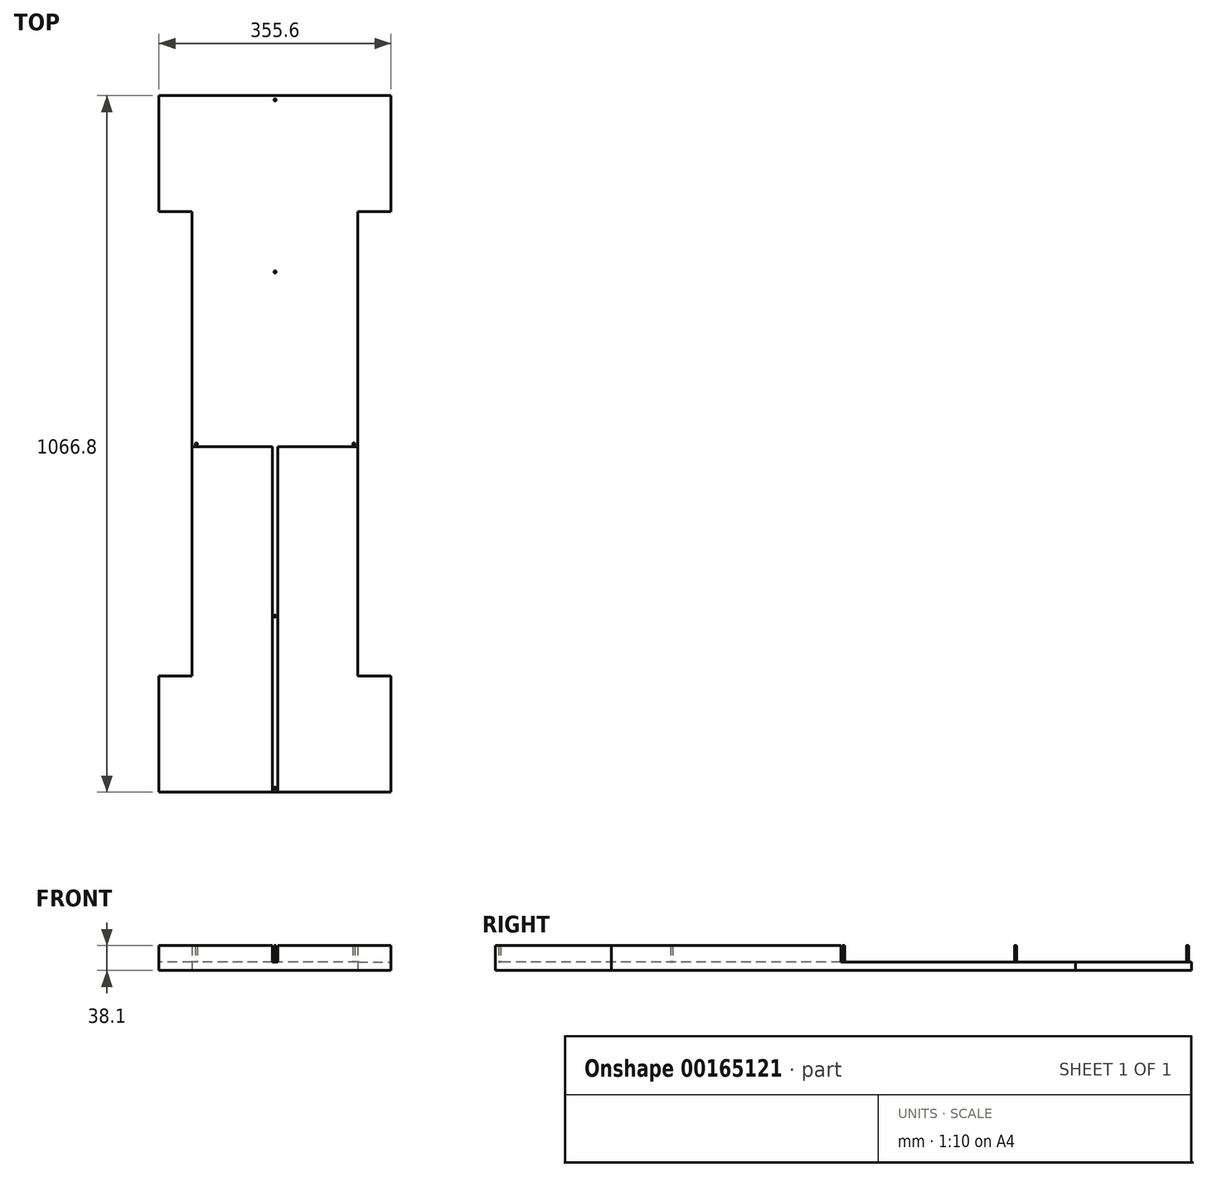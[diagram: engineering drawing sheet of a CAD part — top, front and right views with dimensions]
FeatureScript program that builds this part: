
annotation { "Feature Type Name" : "Feature", "Feature Type Description" : "" }
export const myFeature = defineFeature(function(context is Context, id is Id, definition is map)
    precondition{}
    {
        {
            var Q0;
            Q0=qCreatedBy(makeId("Top.planeOp"),FACE);
            var sketch = newSketch(context, id + "F0", { "sketchPlane" : qUnion([Q0])});
            skLineSegment(sketch, "E0", {"start": v(-127, 0) * mm, "end": v(127, 0) * mm, "construction": true});
            skLineSegment(sketch, "E1.left", {"start": v(-127, -355.6) * mm, "end": v(-127, 355.6) * mm});
            skLineSegment(sketch, "E1.right", {"start": v(127, -355.6) * mm, "end": v(127, 355.6) * mm});
            skLineSegment(sketch, "E2.bottom", {"start": v(-127, 355.6) * mm, "end": v(-177.8, 355.6) * mm});
            skLineSegment(sketch, "E2.top", {"start": v(177.8, 533.4) * mm, "end": v(-177.8, 533.4) * mm});
            skLineSegment(sketch, "E2.left", {"start": v(177.8, 355.6) * mm, "end": v(177.8, 533.4) * mm});
            skLineSegment(sketch, "E2.right", {"start": v(-177.8, 355.6) * mm, "end": v(-177.8, 533.4) * mm});
            skLineSegment(sketch, "E3", {"start": v(0, 0) * mm, "end": v(0, 533.4) * mm, "construction": true});
            skLineSegment(sketch, "E4", {"start": v(127, 355.6) * mm, "end": v(177.8, 355.6) * mm});
            skLineSegment(sketch, "E5", {"start": v(0, 0) * mm, "end": v(0, -533.4) * mm, "construction": true});
            skPoint(sketch, "E6.middle", {"position": v(0, 0) * mm});
            skLineSegment(sketch, "E7", {"start": v(-177.8, 444.5) * mm, "end": v(0, 444.5) * mm, "construction": true});
            skLineSegment(sketch, "E8", {"start": v(-127, -355.6) * mm, "end": v(-177.8, -355.6) * mm});
            skLineSegment(sketch, "E9", {"start": v(-177.8, -355.6) * mm, "end": v(-177.8, -533.4) * mm});
            skLineSegment(sketch, "E10", {"start": v(-177.8, -533.4) * mm, "end": v(177.8, -533.4) * mm});
            skLineSegment(sketch, "E11", {"start": v(177.8, -533.4) * mm, "end": v(177.8, -355.6) * mm});
            skLineSegment(sketch, "E12", {"start": v(177.8, -355.6) * mm, "end": v(127, -355.6) * mm});
            skSolve(sketch);
        }
        {
            var Q0;
            Q0=qSketchRegion(id+"F0",true);
            extrude(context, id + "F1", {"entities" : qUnion([Q0]), "depth" : 12.7 * mm});
        }
        {
            var Q0;
            Q0=makeQuery(id+"F1.opExtrude","CAP_FACE",FACE,{"disambiguationData":[OSD([sQuery(id+"F0.wireOp",EDGE,"E1.left"),sQuery(id+"F0.wireOp",EDGE,"E1.right"),sQuery(id+"F0.wireOp",EDGE,"E2.bottom"),sQuery(id+"F0.wireOp",EDGE,"E2.top"),sQuery(id+"F0.wireOp",EDGE,"E2.left"),sQuery(id+"F0.wireOp",EDGE,"E2.right"),sQuery(id+"F0.wireOp",EDGE,"E4"),sQuery(id+"F0.wireOp",EDGE,"E8"),sQuery(id+"F0.wireOp",EDGE,"E9"),sQuery(id+"F0.wireOp",EDGE,"E10"),sQuery(id+"F0.wireOp",EDGE,"E11"),sQuery(id+"F0.wireOp",EDGE,"E12")])],"isStart":false});
            var sketch = newSketch(context, id + "F2", { "sketchPlane" : qUnion([Q0])});
            skLineSegment(sketch, "E13", {"start": v(0, 533.4) * mm, "end": v(0, 527.05) * mm, "construction": true});
            skLineSegment(sketch, "E14", {"start": v(-127, 0) * mm, "end": v(-120.65, 0) * mm, "construction": true});
            skLineSegment(sketch, "E15", {"start": v(-120.65, 0) * mm, "end": v(120.65, 0) * mm, "construction": true});
            skLineSegment(sketch, "E16", {"start": v(120.65, 0) * mm, "end": v(127, 0) * mm, "construction": true});
            skLineSegment(sketch, "E17", {"start": v(0, 527.05) * mm, "end": v(0, 263.53) * mm, "construction": true});
            skLineSegment(sketch, "E18", {"start": v(0, 263.53) * mm, "end": v(0, 0) * mm, "construction": true});
            skLineSegment(sketch, "E19", {"start": v(0, 0) * mm, "end": v(0, -263.53) * mm, "construction": true});
            skLineSegment(sketch, "E20", {"start": v(0, -263.53) * mm, "end": v(0, -527.05) * mm, "construction": true});
            skLineSegment(sketch, "E21", {"start": v(0, -527.05) * mm, "end": v(0, -533.4) * mm, "construction": true});
            skCircle(sketch, "E22", {"center": v(0, 263.53) * mm, "radius": 1.73 * mm});
            skCircle(sketch, "E23", {"center": v(-120.65, 0) * mm, "radius": 1.73 * mm});
            skCircle(sketch, "E24", {"center": v(120.65, 0) * mm, "radius": 1.73 * mm});
            skCircle(sketch, "E25", {"center": v(0, 527.05) * mm, "radius": 1.73 * mm});
            skCircle(sketch, "E26", {"center": v(0, -263.53) * mm, "radius": 1.73 * mm});
            skCircle(sketch, "E27", {"center": v(0, -527.05) * mm, "radius": 1.73 * mm});
            skLineSegment(sketch, "E28", {"start": v(3.97, -533.4) * mm, "end": v(-3.97, -533.4) * mm, "construction": true});
            skLineSegment(sketch, "E29", {"start": v(127, -3.97) * mm, "end": v(127, 3.97) * mm, "construction": true});
            skLineSegment(sketch, "E30", {"start": v(3.97, 533.4) * mm, "end": v(-3.97, 533.4) * mm, "construction": true});
            skLineSegment(sketch, "E31", {"start": v(-127, -3.97) * mm, "end": v(-127, 3.97) * mm, "construction": true});
            skLineSegment(sketch, "E32.top", {"start": v(-3.97, -3.97) * mm, "end": v(-127, -3.97) * mm});
            skLineSegment(sketch, "E32.left", {"start": v(-3.97, -533.4) * mm, "end": v(-3.97, -3.97) * mm});
            skLineSegment(sketch, "E33.bottom", {"start": v(-127, 3.97) * mm, "end": v(-3.97, 3.97) * mm});
            skLineSegment(sketch, "E33.right", {"start": v(-3.97, 3.97) * mm, "end": v(-3.97, 533.4) * mm});
            skLineSegment(sketch, "E34.top", {"start": v(3.97, 3.97) * mm, "end": v(127, 3.97) * mm});
            skLineSegment(sketch, "E34.left", {"start": v(3.97, 533.4) * mm, "end": v(3.97, 3.97) * mm});
            skLineSegment(sketch, "E35.bottom", {"start": v(127, -3.97) * mm, "end": v(3.97, -3.97) * mm});
            skLineSegment(sketch, "E35.right", {"start": v(3.97, -3.97) * mm, "end": v(3.97, -533.4) * mm});
            skSolve(sketch);
        }
        {
            var Q0;
            Q0 = qSketchRegion(id + "F2", true);
            var Q1;
            {var subQ3=sQuery(id+"F2.wireOp",EDGE,"E35.bottom");Q1=makeQuery(id+"F2.imprint","IMPRINT",FACE,{"disambiguationData":[TD([[makeQuery(id+"F2.imprint","IMPRINT",EDGE,{"derivedFrom":subQ3}),1.0]])]});}
            var Q2;
            {var subQ4=sQuery(id+"F2.wireOp",EDGE,"E32.top");Q2=makeQuery(id+"F2.imprint","IMPRINT",FACE,{"disambiguationData":[TD([[makeQuery(id+"F2.imprint","IMPRINT",EDGE,{"derivedFrom":subQ4}),1.0]])]});}
            extrude(context, id + "F3", {"entities" : qUnion([Q0, Q1, Q2]), "operationType" : NewBodyOperationType.ADD, "depth" : 25.4 * mm});
        }
    });
